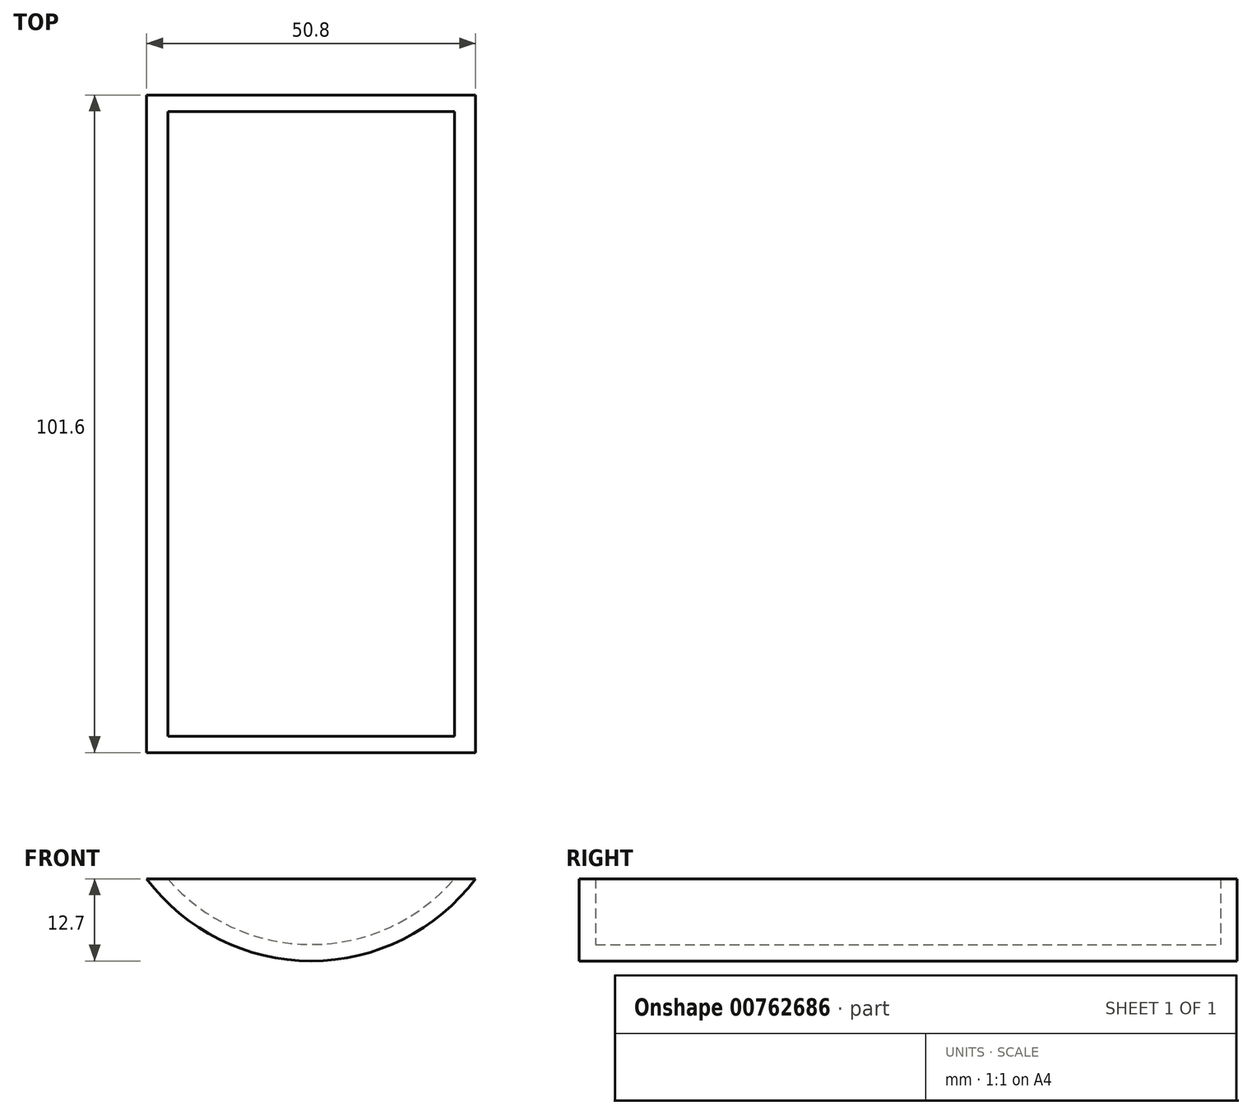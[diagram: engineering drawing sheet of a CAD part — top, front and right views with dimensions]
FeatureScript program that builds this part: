
annotation { "Feature Type Name" : "Feature", "Feature Type Description" : "" }
export const myFeature = defineFeature(function(context is Context, id is Id, definition is map)
    precondition{}
    {
        {
            var Q0;
            Q0=qCreatedBy(makeId("Front.planeOp"),FACE);
            var sketch = newSketch(context, id + "F0", { "sketchPlane" : qUnion([Q0])});
            skLineSegment(sketch, "E0", {"start": v(-84.83, 16.8) * mm, "end": v(-34.03, 16.8) * mm});
            skLineSegment(sketch, "E1", {"start": v(-59.43, 16.8) * mm, "end": v(-59.43, 4.1) * mm});
            skArc(sketch, "E2", {"start": v(-84.83, 16.8) * mm, "mid": v(-59.43, 4.1) * mm, "end": v(-34.03, 16.8) * mm});
            skSolve(sketch);
        }
        {
            var Q0;
            {var subQ3=sQuery(id+"F0.wireOp",EDGE,"E1");Q0=makeQuery(id+"F0.imprint","IMPRINT",FACE,{"disambiguationData":[TD([[makeQuery(id+"F0.imprint","IMPRINT",EDGE,{"derivedFrom":subQ3}),-1.0]])]});}
            var Q1;
            {var subQ3=sQuery(id+"F0.wireOp",EDGE,"E1");Q1=makeQuery(id+"F0.imprint","IMPRINT",FACE,{"disambiguationData":[TD([[makeQuery(id+"F0.imprint","IMPRINT",EDGE,{"derivedFrom":subQ3}),1.0]])]});}
            extrude(context, id + "F1", {"entities" : qUnion([Q0, Q1]), "depth" : 101.6 * mm, "offsetDistance" : 25.4 * mm});
        }
        {
            var Q0;
            Q0=makeQuery(id+"F1.opExtrude","SWEPT_FACE",FACE,{"disambiguationData":[OSD([sQuery(id+"F0.wireOp",EDGE,"E0")])]});
            shell(context, id + "F2", {"entities" : qUnion([Q0]), "thickness" : 2.54 * mm});
        }
    });
